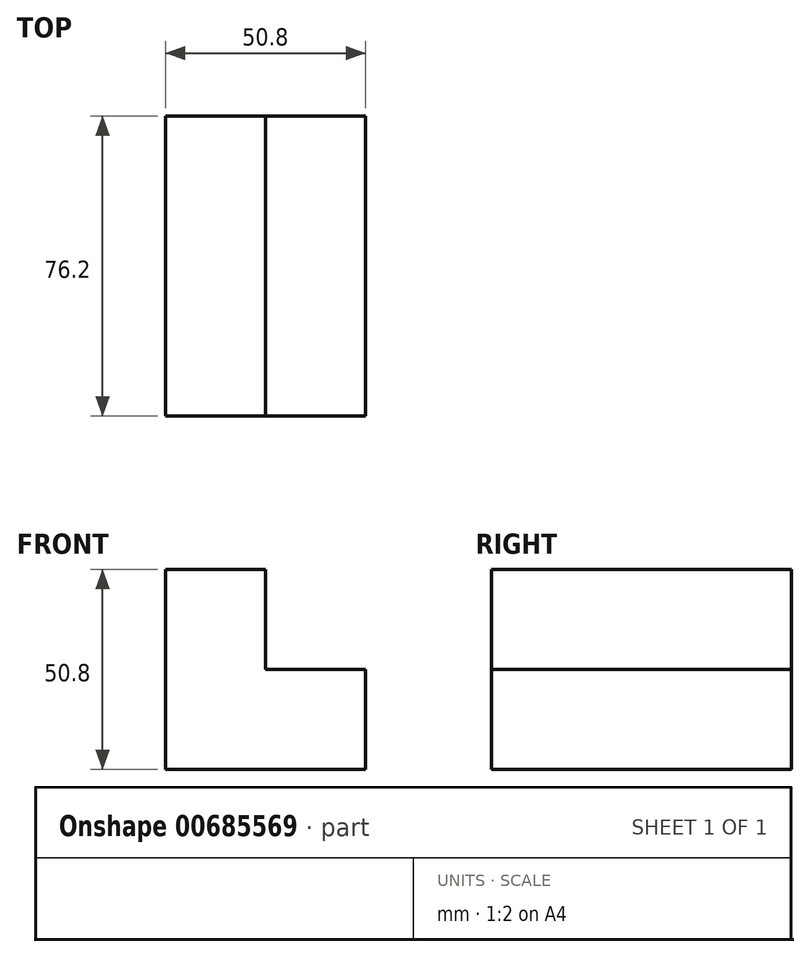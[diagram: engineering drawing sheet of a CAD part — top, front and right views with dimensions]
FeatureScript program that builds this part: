
annotation { "Feature Type Name" : "Feature", "Feature Type Description" : "" }
export const myFeature = defineFeature(function(context is Context, id is Id, definition is map)
    precondition{}
    {
        {
            var Q0;
            Q0=qCreatedBy(makeId("Front.planeOp"),FACE);
            var sketch = newSketch(context, id + "F0", { "sketchPlane" : qUnion([Q0])});
            skLineSegment(sketch, "E0", {"start": v(-42.62, 66.89) * mm, "end": v(-42.62, 16.09) * mm});
            skLineSegment(sketch, "E1", {"start": v(-42.62, 16.09) * mm, "end": v(8.18, 16.09) * mm});
            skLineSegment(sketch, "E2", {"start": v(8.18, 16.09) * mm, "end": v(8.18, 41.49) * mm});
            skLineSegment(sketch, "E3", {"start": v(8.18, 41.49) * mm, "end": v(-17.22, 41.49) * mm});
            skLineSegment(sketch, "E4", {"start": v(-17.22, 41.49) * mm, "end": v(-17.22, 66.89) * mm});
            skLineSegment(sketch, "E5", {"start": v(-17.22, 66.89) * mm, "end": v(-42.62, 66.89) * mm});
            skSolve(sketch);
        }
        {
            var Q0;
            Q0 = qSketchRegion(id + "F0", true);
            extrude(context, id + "F1", {"entities" : qUnion([Q0]), "depth" : 76.2 * mm, "offsetDistance" : 25.4 * mm});
        }
    });
